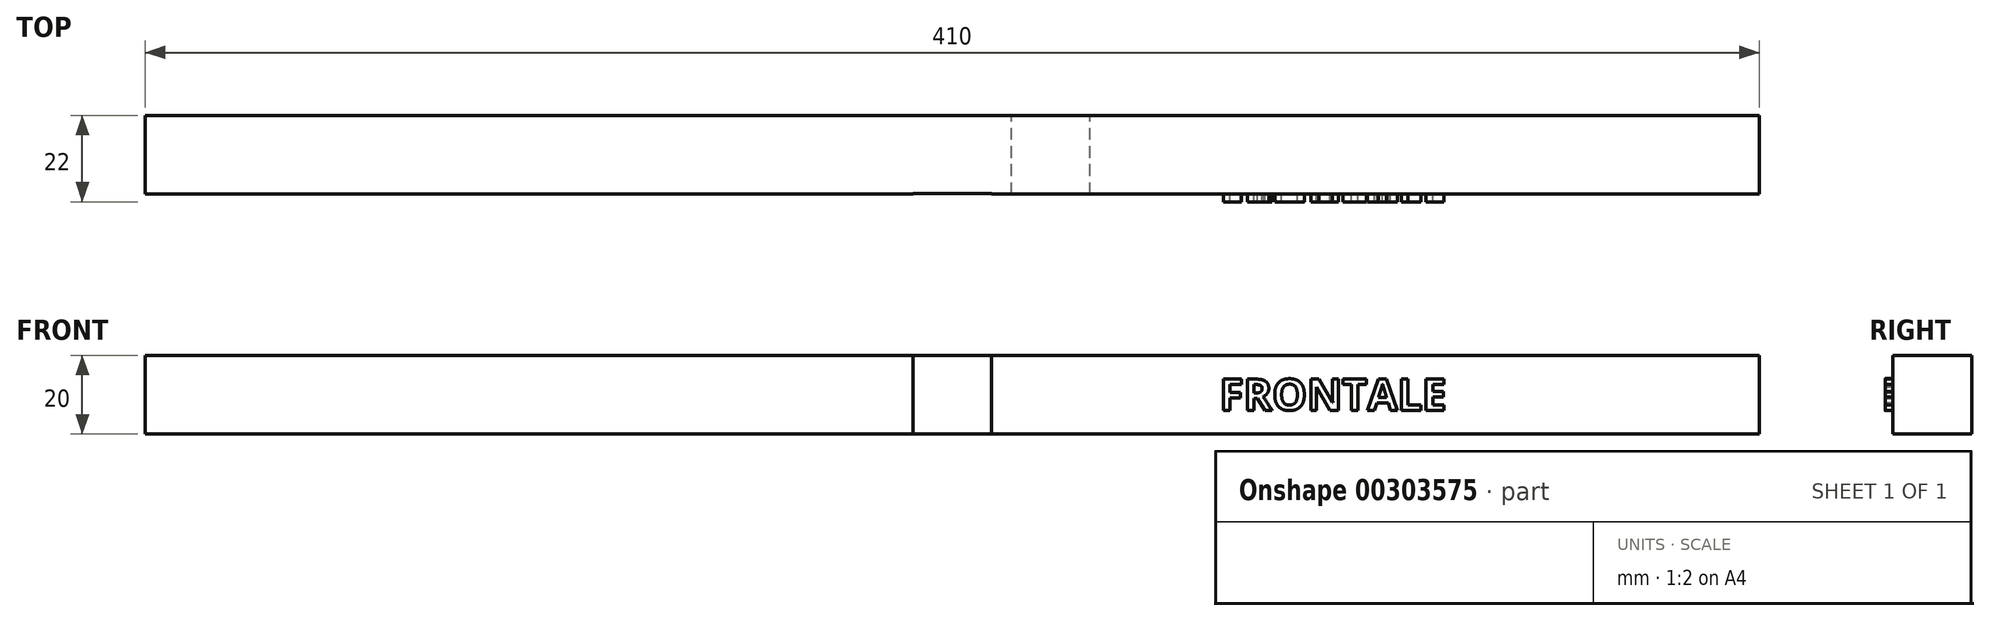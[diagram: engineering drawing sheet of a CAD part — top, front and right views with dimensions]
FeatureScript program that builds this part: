
annotation { "Feature Type Name" : "Feature", "Feature Type Description" : "" }
export const myFeature = defineFeature(function(context is Context, id is Id, definition is map)
    precondition{}
    {
        {
            var Q0;
            Q0=qCreatedBy(makeId("Front.planeOp"),FACE);
            var sketch = newSketch(context, id + "F0", { "sketchPlane" : qUnion([Q0])});
            skLineSegment(sketch, "E0.bottom", {"start": v(264.99, 5.9) * mm, "end": v(-145.01, 5.9) * mm});
            skLineSegment(sketch, "E0.top", {"start": v(264.99, 25.9) * mm, "end": v(-145.01, 25.9) * mm});
            skLineSegment(sketch, "E0.left", {"start": v(264.99, 5.9) * mm, "end": v(264.99, 25.9) * mm});
            skLineSegment(sketch, "E0.right", {"start": v(-145.01, 5.9) * mm, "end": v(-145.01, 25.9) * mm});
            skPoint(sketch, "E0.middle", {"position": v(59.99, 15.9) * mm});
            skSolve(sketch);
        }
        {
            var Q0;
            Q0=makeQuery(id+"F0.imprint","IMPRINT",FACE,{"disambiguationData":[TD([[makeQuery(id+"F0.imprint","IMPRINT",EDGE,{"derivedFrom":sQuery(id+"F0.wireOp",EDGE,"E0.bottom")}),-1.0]])]});
            extrude(context, id + "F1", {"entities" : qUnion([Q0]), "depth" : 20 * mm});
        }
        {
            var Q0;
            Q0=makeQuery(id+"F1.opExtrude","CAP_FACE",FACE,{"disambiguationData":[OSD([sQuery(id+"F0.wireOp",EDGE,"E0.bottom"),sQuery(id+"F0.wireOp",EDGE,"E0.top"),sQuery(id+"F0.wireOp",EDGE,"E0.left"),sQuery(id+"F0.wireOp",EDGE,"E0.right")])],"isStart":false});
            var sketch = newSketch(context, id + "F2", { "sketchPlane" : qUnion([Q0])});
            skLineSegment(sketch, "E1", {"start": v(-145.01, 25.9) * mm, "end": v(264.99, 5.9) * mm, "construction": true});
            skLineSegment(sketch, "E2", {"start": v(264.99, 5.9) * mm, "end": v(264.99, 25.9) * mm, "construction": true});
            skLineSegment(sketch, "E3", {"start": v(264.99, 25.9) * mm, "end": v(-145.01, 5.9) * mm, "construction": true});
            skPoint(sketch, "E4", {"position": v(59.99, 15.9) * mm});
            skLineSegment(sketch, "E5.bottom", {"start": v(69.99, 25.9) * mm, "end": v(49.99, 25.9) * mm});
            skLineSegment(sketch, "E5.left", {"start": v(69.99, 25.9) * mm, "end": v(69.99, 5.9) * mm});
            skLineSegment(sketch, "E5.right", {"start": v(49.99, 25.9) * mm, "end": v(49.99, 5.9) * mm});
            skSolve(sketch);
        }
        {
            var Q0;
            Q0=makeQuery(id+"F1.opExtrude","CAP_FACE",FACE,{"disambiguationData":[OSD([sQuery(id+"F0.wireOp",EDGE,"E0.bottom"),sQuery(id+"F0.wireOp",EDGE,"E0.top"),sQuery(id+"F0.wireOp",EDGE,"E0.left"),sQuery(id+"F0.wireOp",EDGE,"E0.right")])],"isStart":false});
            var sketch = newSketch(context, id + "F3", { "sketchPlane" : qUnion([Q0])});
            skText(sketch, "E6", { "text": "FRONTALE", "fontName": "OpenSans-Bold.ttf"});
            const initialGuessF3  = {"E6": [0.12787, 0.01197, 1, 0, 0.00797]};
            skSetInitialGuess(sketch, initialGuessF3);
            skSolve(sketch);
        }
        {
            var Q0;
            Q0 = qSketchRegion(id + "F3", true);
            extrude(context, id + "F4", {"entities" : qUnion([Q0]), "operationType" : NewBodyOperationType.ADD, "depth" : 2 * mm});
        }
        {
            var Q0;
            Q0=makeQuery(id+"F1.opExtrude","SWEPT_FACE",FACE,{"disambiguationData":[OSD([sQuery(id+"F0.wireOp",EDGE,"E0.bottom")])]});
            var sketch = newSketch(context, id + "F5", { "sketchPlane" : qUnion([Q0])});
            skLineSegment(sketch, "E7.0", {"start": v(74.99, 20) * mm, "end": v(74.99, 0) * mm});
            skLineSegment(sketch, "E8.0", {"start": v(94.99, 20) * mm, "end": v(94.99, 0) * mm});
            skLineSegment(sketch, "E9", {"start": v(74.99, 0) * mm, "end": v(94.99, 0) * mm});
            skSolve(sketch);
        }
        {
            var Q0;
            Q0=makeQuery(id+"F2.imprint","IMPRINT",FACE,{"disambiguationData":[TD([[makeQuery(id+"F2.imprint","IMPRINT",EDGE,{"derivedFrom":sQuery(id+"F2.wireOp",EDGE,"E5.bottom")}),1.0]])]});
            extrude(context, id + "F6", {"entities" : qUnion([Q0]), "operationType" : NewBodyOperationType.REMOVE, "oppositeDirection" : true, "depth" : 0.1 * mm});
        }
        {
            var Q0;
            {var subQ0=sQuery(id+"F5.wireOp",EDGE,"E7.0");Q0=makeQuery(id+"F5.imprint","IMPRINT",FACE,{"disambiguationData":[TD([[makeQuery(id+"F5.imprint","IMPRINT",EDGE,{"derivedFrom":subQ0}),1.0]])]});}
            extrude(context, id + "F7", {"entities" : qUnion([Q0]), "operationType" : NewBodyOperationType.REMOVE, "oppositeDirection" : true, "depth" : 0.1 * mm});
        }
    });
